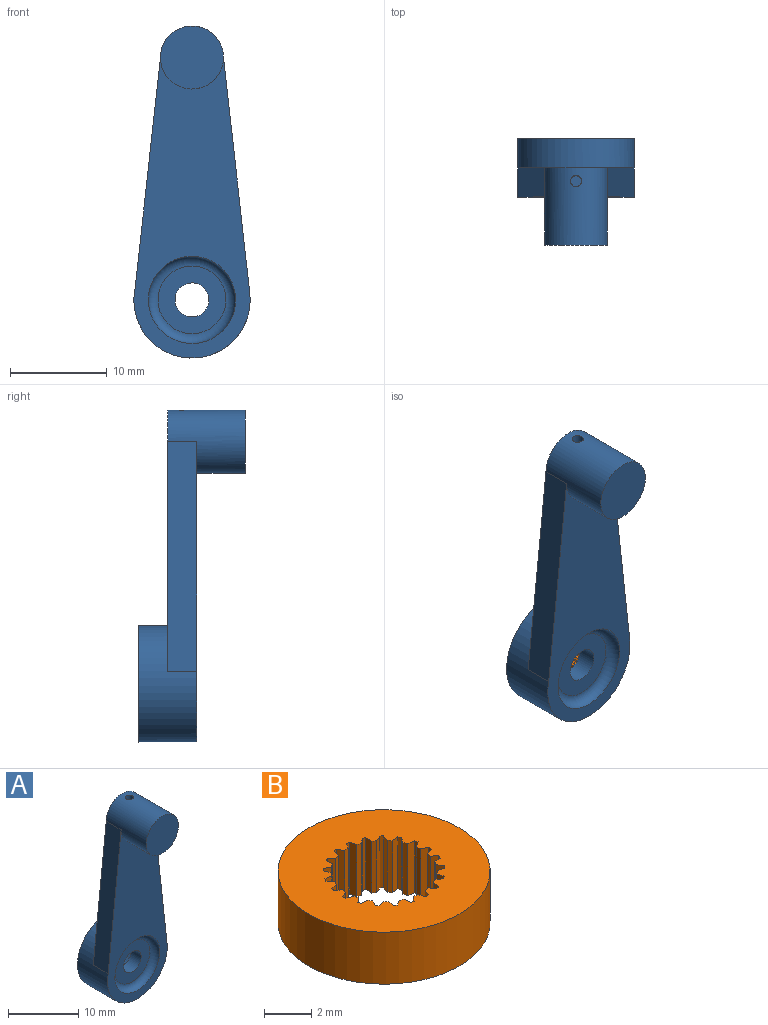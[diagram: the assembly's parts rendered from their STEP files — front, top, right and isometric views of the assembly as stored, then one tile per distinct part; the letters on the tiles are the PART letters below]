
ASSEMBLY  parts=2 mates=1
PART A: 15 faces, bbox 12x11x34.3 mm
  f0: cylinder r=4.5mm len=9mm, axis (0,1,0), area 84.8mm2, adj f3,f11
  f1: cylinder r=6mm len=12mm, axis (0,1,0), area 175.6mm2, adj f2,f3,f4,f5,f6
  f2: plane 31x12mm, normal (0,-1,0), area 208.1mm2, adj f1,f4,f5,f7,f12
  f3: plane 12x12mm, normal (0,1,0), area 49.5mm2, adj f0,f1
  f4: plane 24.34x3mm, normal (0.99,0,0.11), area 73.5mm2, adj f1,f2,f6,f7
  f5: plane 23.7x3mm, normal (-0.99,0,0.11), area 71.5mm2, adj f1,f2,f6,f7
  f6: plane 27.59x11.82mm, normal (0,1,0), area 191.8mm2, adj f1,f4,f5,f7
  f7: cylinder r=3.25mm len=8mm, axis (0,1,0), area 131.7mm2, adj f2,f4,f5,f6,f8,f13
  f8: plane 6.5x6.5mm, normal (0,-1,0), area 33.2mm2, adj f7
  f9: cylinder r=1.75mm len=3.5mm, axis (0,1,0), area 22mm2, adj f10,f11
  f10: plane 7x7mm, normal (0,-1,0), area 28.9mm2, adj f9,f12
  f11: plane 9x9mm, normal (0,1,0), area 54mm2, adj f0,f9
  f12: torus R=3.5mm, axis (0,-1,0), area 40.8mm2, adj f2,f10
  f13: cylinder r=0.57mm len=24.25mm, axis (0,0,1), area 87.5mm2, adj f7,f14
  f14: plane 1.15x1.15mm, normal (0,0,1), area 1mm2, adj f13
PART B: 87 faces, bbox 9x9x2.7 mm
  f0: cylinder r=2.58mm len=2.7mm, axis (0,0,-1), area 0.5mm2, adj f22,f24,f25,f57
  f1: cylinder r=2.58mm len=2.7mm, axis (0,0,-1), area 0.5mm2, adj f24,f25,f55,f56
  f2: cylinder r=2.58mm len=2.7mm, axis (0,0,-1), area 0.5mm2, adj f24,f25,f53,f54
  f3: cylinder r=2.58mm len=2.7mm, axis (0,0,-1), area 0.5mm2, adj f24,f25,f51,f52
  f4: cylinder r=2.58mm len=2.7mm, axis (0,0,-1), area 0.5mm2, adj f24,f25,f49,f50
  f5: cylinder r=2.58mm len=2.7mm, axis (0,0,-1), area 0.5mm2, adj f24,f25,f47,f48
  f6: cylinder r=2.58mm len=2.7mm, axis (0,0,-1), area 0.5mm2, adj f24,f25,f45,f46
  f7: cylinder r=2.58mm len=2.7mm, axis (0,0,-1), area 0.5mm2, adj f24,f25,f43,f44
  f8: cylinder r=2.58mm len=2.7mm, axis (0,0,-1), area 0.5mm2, adj f24,f25,f41,f42
  f9: cylinder r=2.58mm len=2.7mm, axis (0,0,-1), area 0.5mm2, adj f24,f25,f39,f40
  f10: cylinder r=2.58mm len=2.7mm, axis (0,0,-1), area 0.5mm2, adj f24,f25,f37,f38
  f11: cylinder r=2.58mm len=2.7mm, axis (0,0,-1), area 0.5mm2, adj f24,f25,f35,f36
  f12: cylinder r=2.58mm len=2.7mm, axis (0,0,-1), area 0.5mm2, adj f24,f25,f33,f34
  f13: cylinder r=2.58mm len=2.7mm, axis (0,0,-1), area 0.5mm2, adj f24,f25,f31,f32
  f14: cylinder r=2.58mm len=2.7mm, axis (0,0,-1), area 0.5mm2, adj f24,f25,f29,f30
  f15: cylinder r=2.58mm len=2.7mm, axis (0,0,-1), area 0.5mm2, adj f24,f25,f27,f28
  f16: cylinder r=2.58mm len=2.7mm, axis (0,0,-1), area 0.5mm2, adj f24,f25,f26,f64
  f17: cylinder r=2.58mm len=2.7mm, axis (0,0,-1), area 0.5mm2, adj f24,f25,f63,f65
  f18: cylinder r=2.58mm len=2.7mm, axis (0,0,-1), area 0.5mm2, adj f24,f25,f61,f62
  f19: cylinder r=2.58mm len=2.7mm, axis (0,0,-1), area 0.5mm2, adj f24,f25,f58,f60
  f20: plane 2.7x0.31mm, normal (0.86,-0.51,0), area 1mm2, adj f21,f24,f25,f86
  f21: cylinder r=2.58mm len=2.7mm, axis (0,0,-1), area 0.5mm2, adj f20,f24,f25,f59
  f22: plane 2.7x0.31mm, normal (-0.86,-0.51,0), area 1mm2, adj f0,f24,f25,f86
  f23: cylinder r=4.5mm len=9mm, axis (0,0,-1), area 76.3mm2, adj f24,f25
  f24: plane 9x9mm, normal (0,0,1), area 45.6mm2, adj f0,f1,f2,f3,f4,f5,f6,f7
  f25: plane 9x9mm, normal (0,0,-1), area 45.6mm2, adj f0,f1,f2,f3,f4,f5,f6,f7
  f26: plane 2.7x0.3mm, normal (-0.58,0.82,0), area 1mm2, adj f16,f24,f25,f85
  f27: plane 2.7x0.32mm, normal (-0.45,-0.89,0), area 1mm2, adj f15,f24,f25,f85
  f28: plane 2.7x0.34mm, normal (-0.31,0.95,0), area 1mm2, adj f15,f24,f25,f84
  f29: plane 2.7x0.26mm, normal (-0.69,-0.72,0), area 1mm2, adj f14,f24,f25,f84
  f30: plane 2.7x0.36mm, normal (-0.02,1,0), area 1mm2, adj f14,f24,f25,f83
  f31: plane 2.7x0.32mm, normal (-0.87,-0.49,0), area 1mm2, adj f13,f24,f25,f83
  f32: plane 2.7x0.35mm, normal (0.28,0.96,0), area 1mm2, adj f13,f24,f25,f82
  f33: plane 2.7x0.35mm, normal (-0.98,-0.21,0), area 1mm2, adj f12,f24,f25,f82
  f34: plane 2.7x0.3mm, normal (0.55,0.84,0), area 1mm2, adj f12,f24,f25,f81
  f35: plane 2.7x0.36mm, normal (-1,0.09,0), area 1mm2, adj f11,f24,f25,f81
  f36: plane 2.7x0.28mm, normal (0.77,0.64,0), area 1mm2, adj f11,f24,f25,f80
  f37: plane 2.7x0.33mm, normal (-0.92,0.38,0), area 1mm2, adj f10,f24,f25,f80
  f38: plane 2.7x0.33mm, normal (0.92,0.38,0), area 1mm2, adj f10,f24,f25,f79
  f39: plane 2.7x0.28mm, normal (-0.77,0.64,0), area 1mm2, adj f9,f24,f25,f79
  f40: plane 2.7x0.36mm, normal (1,0.09,0), area 1mm2, adj f9,f24,f25,f78
  f41: plane 2.7x0.3mm, normal (-0.55,0.84,0), area 1mm2, adj f8,f24,f25,f78
  f42: plane 2.7x0.35mm, normal (0.98,-0.21,0), area 1mm2, adj f8,f24,f25,f77
  f43: plane 2.7x0.35mm, normal (-0.28,0.96,0), area 1mm2, adj f7,f24,f25,f77
  f44: plane 2.7x0.32mm, normal (0.87,-0.49,0), area 1mm2, adj f7,f24,f25,f76
  f45: plane 2.7x0.36mm, normal (0.02,1,0), area 1mm2, adj f6,f24,f25,f76
  f46: plane 2.7x0.26mm, normal (0.69,-0.72,0), area 1mm2, adj f6,f24,f25,f75
  f47: plane 2.7x0.34mm, normal (0.31,0.95,0), area 1mm2, adj f5,f24,f25,f75
  f48: plane 2.7x0.32mm, normal (0.45,-0.89,0), area 1mm2, adj f5,f24,f25,f74
  f49: plane 2.7x0.3mm, normal (0.58,0.82,0), area 1mm2, adj f4,f24,f25,f74
  f50: plane 2.7x0.36mm, normal (0.17,-0.99,0), area 1mm2, adj f4,f24,f25,f73
  f51: plane 2.7x0.29mm, normal (0.79,0.61,0), area 1mm2, adj f3,f24,f25,f73
  f52: plane 2.7x0.36mm, normal (-0.13,-0.99,0), area 1mm2, adj f3,f24,f25,f72
  f53: plane 2.7x0.34mm, normal (0.94,0.35,0), area 1mm2, adj f2,f24,f25,f72
  f54: plane 2.7x0.33mm, normal (-0.42,-0.91,0), area 1mm2, adj f2,f24,f25,f71
  f55: plane 2.7x0.36mm, normal (1,0.06,0), area 1mm2, adj f1,f24,f25,f71
  f56: plane 2.7x0.27mm, normal (-0.67,-0.74,0), area 1mm2, adj f1,f24,f25,f70
  f57: plane 2.7x0.35mm, normal (0.97,-0.24,0), area 1mm2, adj f0,f24,f25,f70
  f58: plane 2.7x0.27mm, normal (0.67,-0.74,0), area 1mm2, adj f19,f24,f25,f69
  f59: plane 2.7x0.35mm, normal (-0.97,-0.24,0), area 1mm2, adj f21,f24,f25,f69
  f60: plane 2.7x0.36mm, normal (-1,0.06,0), area 1mm2, adj f19,f24,f25,f68
  f61: plane 2.7x0.33mm, normal (0.42,-0.91,0), area 1mm2, adj f18,f24,f25,f68
  f62: plane 2.7x0.34mm, normal (-0.94,0.35,0), area 1mm2, adj f18,f24,f25,f67
  f63: plane 2.7x0.36mm, normal (0.13,-0.99,0), area 1mm2, adj f17,f24,f25,f67
  f64: plane 2.7x0.36mm, normal (-0.17,-0.99,0), area 1mm2, adj f16,f24,f25,f66
  f65: plane 2.7x0.29mm, normal (-0.79,0.61,0), area 1mm2, adj f17,f24,f25,f66
  f66: cylinder r=2.25mm len=2.7mm, axis (0,0,1), area 0.6mm2, adj f24,f25,f64,f65
  f67: cylinder r=2.25mm len=2.7mm, axis (0,0,1), area 0.6mm2, adj f24,f25,f62,f63
  f68: cylinder r=2.25mm len=2.7mm, axis (0,0,1), area 0.6mm2, adj f24,f25,f60,f61
  f69: cylinder r=2.25mm len=2.7mm, axis (0,0,1), area 0.6mm2, adj f24,f25,f58,f59
  f70: cylinder r=2.25mm len=2.7mm, axis (0,0,1), area 0.6mm2, adj f24,f25,f56,f57
  f71: cylinder r=2.25mm len=2.7mm, axis (0,0,1), area 0.6mm2, adj f24,f25,f54,f55
  f72: cylinder r=2.25mm len=2.7mm, axis (0,0,1), area 0.6mm2, adj f24,f25,f52,f53
  f73: cylinder r=2.25mm len=2.7mm, axis (0,0,1), area 0.6mm2, adj f24,f25,f50,f51
  f74: cylinder r=2.25mm len=2.7mm, axis (0,0,1), area 0.6mm2, adj f24,f25,f48,f49
  f75: cylinder r=2.25mm len=2.7mm, axis (0,0,1), area 0.6mm2, adj f24,f25,f46,f47
  f76: cylinder r=2.25mm len=2.7mm, axis (0,0,1), area 0.6mm2, adj f24,f25,f44,f45
  f77: cylinder r=2.25mm len=2.7mm, axis (0,0,1), area 0.6mm2, adj f24,f25,f42,f43
  f78: cylinder r=2.25mm len=2.7mm, axis (0,0,1), area 0.6mm2, adj f24,f25,f40,f41
  f79: cylinder r=2.25mm len=2.7mm, axis (0,0,1), area 0.6mm2, adj f24,f25,f38,f39
  f80: cylinder r=2.25mm len=2.7mm, axis (0,0,1), area 0.6mm2, adj f24,f25,f36,f37
  f81: cylinder r=2.25mm len=2.7mm, axis (0,0,1), area 0.6mm2, adj f24,f25,f34,f35
  f82: cylinder r=2.25mm len=2.7mm, axis (0,0,1), area 0.6mm2, adj f24,f25,f32,f33
  f83: cylinder r=2.25mm len=2.7mm, axis (0,0,1), area 0.6mm2, adj f24,f25,f30,f31
  f84: cylinder r=2.25mm len=2.7mm, axis (0,0,1), area 0.6mm2, adj f24,f25,f28,f29
  f85: cylinder r=2.25mm len=2.7mm, axis (0,0,1), area 0.6mm2, adj f24,f25,f26,f27
  f86: cylinder r=2.25mm len=2.7mm, axis (0,0,1), area 0.6mm2, adj f20,f22,f24,f25
PLACE A at identity
PLACE B rot(axis=(-1,0,0),90deg) t=(0,0,0)mm
MATE fastened B.f0 <-> A.f0  axis (0,-1,0) through (0,0,0)mm
